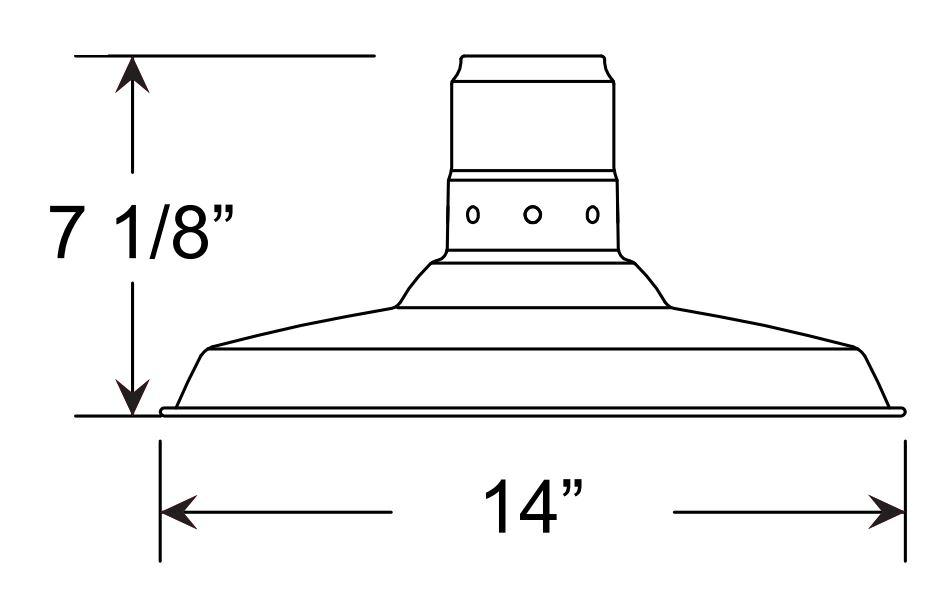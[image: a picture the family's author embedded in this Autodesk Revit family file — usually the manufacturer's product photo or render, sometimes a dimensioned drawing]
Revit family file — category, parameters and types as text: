
# Revit family: OSDD_LED
name_source: partatom
category: Lighting Fixtures
units: mm (PartAtom-declared; Revit-internal decimal feet)

## family parameters
Always vertical = Yes
Cut with Voids When Loaded = No
Light Source = Yes
OmniClass Number = 23.80.70.00
OmniClass Title = Lighting
Part Type = Normal
Room Calculation Point = No
Round Connector Dimension = Use Diameter
Shared = No
Work Plane-Based = No

## types (3) — shared parameters
Apparent Load = 37 VA
Body Colour = Spun aluminium
Body Material = body
Bulb = BULB
CRI = >90
Color Filter = 16777215
Construction Material = Heavy Duty spun aluminum.
Default Elevation = 0' - 0"
Description = 120-277 Voltage
Dimming = 1%
Dimming Lamp Color Temperature Shift = <None>
Efficiency = 65-125 lumens per watt
GLASS = Glass
Inside body material = INSIDE BODY MATERIAL
Lamp = LED
Life = L70 50,000 hours
Load Classification = Lighting
Manufacturer = ANP Lighting
Photometric Web File = OSDD30M037LDDW35K.ies
Power Factor = 1
Tilt Angle = 90.00°
URL = https://www.anplighting.com
Warranty = 5 year limited warranty
Wattage Comments = 37W

## per-type parameters (varying)
| type | Fixture Diameter | Fixture Height | OSDD22 | OSDD30 | OSDD36 | Voltage | Weight |
| OSDD22 | 1' - 10" | 1' - 1" | Yes | No | No | 120 V | 18.0 lb |
| OSDD30 | 2' - 6" | 1' - 7" | No | Yes | No | 120 V | 21.0 lb |
| OSDD36 | 3' - 0" | 1' - 9" | No | No | Yes | 277 V | 23.0 lb |

note: column(s) folded — value = type name in every type: Model

## geometry (parser evidence)
native form markers: Sweep x30
no freeform markers — native parametric forms only
